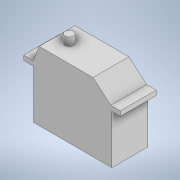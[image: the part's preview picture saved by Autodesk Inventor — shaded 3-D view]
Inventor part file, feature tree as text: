
AUTODESK INVENTOR PART (.ipt)
format: ipt  version: 2020 (Build 240168000, 168)  size: 117,248 bytes
history: native  units: mm
features: extrude x2, sketch x2
ambient origin geometry x8: Origin, YZ Plane, XZ Plane, XY Plane, X Axis, Y Axis, Z Axis, Center Point
bodies: Solid1 (feature_tree)
feature tree (4):
  extrude  "Extrusion1"  Depth=40.8mm
  extrude  "Extrusion2"  Depth=30.0mm TaperAngle=0.0deg
  sketch  "Sketch1"  dims[d0=65.7mm d1=40.8mm]
  sketch  "Sketch2"  dims[d2=4.0mm d3=30.0mm d4=0.0mm d5=7.0mm d6=15.0mm d7=15.0mm d9=57.5mm d10=6.8mm d11=0.0mm d13=8.0mm d14=8.0mm]
